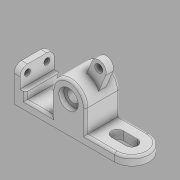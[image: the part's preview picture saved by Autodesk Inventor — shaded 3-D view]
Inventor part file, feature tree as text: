
AUTODESK INVENTOR PART (.ipt)
format: ipt  version: 2020 (Build 240168000, 168)  size: 280,064 bytes
history: native  units: in
note: dims shown in document units (in); Inventor stores cm internally (conversion verified against a paired STEP export)
features: sketch x10, extrude x9, other x2, projected_geometry x2, hole x1, fillet x1
ambient origin geometry x8: Origin, YZ Plane, XZ Plane, XY Plane, X Axis, Y Axis, Z Axis, Center Point
bodies: Body1 (feature_tree), Body2 (feature_tree)
feature tree (25):
  other  "Sólido1"
  extrude  "Base"  Depth=1.75in
  extrude  "RedondeoIzquierda"  Depth=0.81in
  extrude  "RedondeoDerecha"  Depth=0.44in
  extrude  "HuecoDerecha"  Depth=1.62in
  hole  "AgujeroCentral"  [1 undecoded]
  extrude  "HuecosIzquierda"  Depth=0.31in TaperAngle=0.0deg
  extrude  "Protuberancia"  Depth=1.76in
  extrude  "RestoFrontalProtuberancia"  Depth=0.88in
  extrude  "RestoTraseroProtuberancia"  Depth=1.76in
  extrude  "HuecoProtuberancia"  Depth=0.594in
  fillet  "Empalmes"  Radius=1.76in
  sketch  "Boceto1"  dims[d0=0.31in d1=1.75in]
  sketch  "Boceto2"  dims[d2=0.28in d3=0.81in]
  sketch  "Boceto3"  dims[d4=5.48in d5=0.44in]
  sketch  "Boceto4"  dims[d6=2.5in d7=1.62in]
  sketch  "Boceto5"  dims[d8=1.76in d9=1.76in d10=0.0in]
  sketch  "Boceto6"  dims[d11=0.38in d12=0.31in d13=0.0in]
  sketch  "Boceto7"  dims[d14=0.88in d15=1.76in]
  projected_geometry  "Contorno proyectado1"
  projected_geometry  "Contorno proyectado2"
  other  "Sólido2"
  sketch  "Boceto8"  dims[d16=0.88in d17=2.81in]
  sketch  "Boceto9"  dims[d18=2.38in d19=1.76in]
  sketch  "Boceto10"  dims[d20=0.44in d21=0.0in d22=0.594in d23=1.76in d24=0.583in d26=0.75in d27=0.44in d28=0.0in d29=0.609in d30=0.75in d31=1.0in d32=0.25in d33=0.5635in d34=1.0in d35=0.8108in d36=0.312in d37=0.312in d38=0.38in d39=0.38in d40=0.38in d41=0.38in d42=1.37in d43=1.0in d44=0.31in d45=0.0in d48=0.88in d49=1.62in d50=60.0deg d51=0.76in d52=1.76in d53=0.0in d54=0.75in d55=0.0in d56=0.63in d57=0.0in d58=0.406in d59=0.38in d60=0.0in d61=0.12in]
note: 1 required parameter value undecoded (feature->parameter linkage not recoverable at this tier; creation-order binding heuristic only, values carry confidence <= 0.55)
